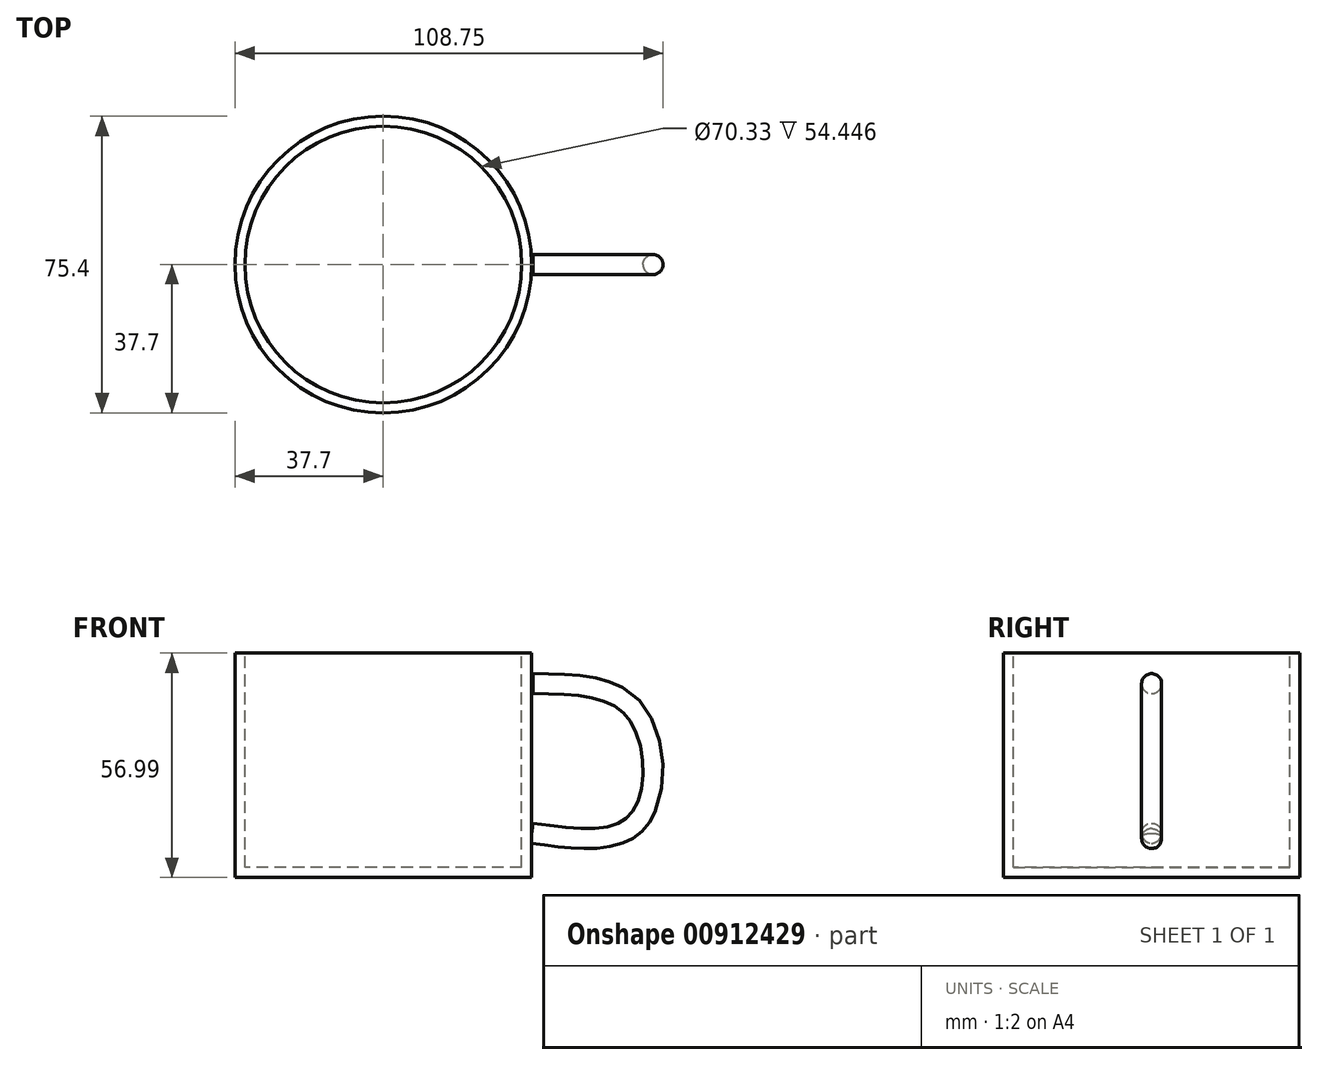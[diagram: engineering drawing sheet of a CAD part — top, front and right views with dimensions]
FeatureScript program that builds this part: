
annotation { "Feature Type Name" : "Feature", "Feature Type Description" : "" }
export const myFeature = defineFeature(function(context is Context, id is Id, definition is map)
    precondition{}
    {
        {
            var Q0;
            Q0=qCreatedBy(makeId("Front.planeOp"),FACE);
            var sketch = newSketch(context, id + "F0", { "sketchPlane" : qUnion([Q0])});
            skLineSegment(sketch, "E0.bottom", {"start": v(0, 64.9) * mm, "end": v(37.7, 64.9) * mm});
            skLineSegment(sketch, "E0.top", {"start": v(0, 7.91) * mm, "end": v(37.7, 7.91) * mm});
            skLineSegment(sketch, "E0.left", {"start": v(0, 64.9) * mm, "end": v(0, 7.91) * mm});
            skLineSegment(sketch, "E0.right", {"start": v(37.7, 64.9) * mm, "end": v(37.7, 7.91) * mm});
            skSolve(sketch);
        }
        {
            var Q0;
            Q0=makeQuery(id+"F0.imprint","IMPRINT",FACE,{"disambiguationData":[TD([[makeQuery(id+"F0.imprint","IMPRINT",EDGE,{"derivedFrom":sQuery(id+"F0.wireOp",EDGE,"E0.bottom")}),-1.0]])]});
            var Q1;
            Q1=sQuery(id+"F0.wireOp",EDGE,"E0.left");
            revolve(context, id + "F1", {"surfaceOperationType" : NewSurfaceOperationType.NEW, "entities" : qUnion([Q0]), "axis" : qUnion([Q1]), "revolveType" : RevolveType.FULL});
        }
        {
            var Q0;
            Q0=makeQuery(id+"F1.opRevolve","SWEPT_FACE",FACE,{"disambiguationData":[OSD([sQuery(id+"F0.wireOp",EDGE,"E0.bottom")])]});
            shell(context, id + "F2", {"entities" : qUnion([Q0]), "thickness" : 2.54 * mm});
        }
        {
            var Q0;
            Q0=qCreatedBy(makeId("Front.planeOp"),FACE);
            var sketch = newSketch(context, id + "F3", { "sketchPlane" : qUnion([Q0])});
            skFitSpline(sketch, "E1", {"points": [v(38, 57.13) * mm, v(64.18, 49.93) * mm, v(64.76, 22.3) * mm, v(37.7, 19.14) * mm], "startDerivative": vector(93.79, -0.65) * mm, "endDerivative": vector(-98.25, 13.93) * mm});
            skSolve(sketch);
        }
        {
            var Q0;
            Q0=sQuery(id+"F3.wireOp",EDGE,"E1");
            var Q1;
            Q1=sQuery(id+"F3.wireOp",VERTEX,"E1.end");
            cPlane(context, id + "F4", {"entities" : qUnion([Q0, Q1]), "cplaneType" : CPlaneType.CURVE_POINT, "offset" : 25.4 * mm, "width" : 152.4 * mm, "height" : 152.4 * mm});
        }
        {
            var Q0;
            Q0=qCreatedBy(id+"F4.planeOp",FACE);
            var sketch = newSketch(context, id + "F5", { "sketchPlane" : qUnion([Q0])});
            skCircle(sketch, "E2", {"center": v(0, 24.24) * mm, "radius": 2.54 * mm});
            skSolve(sketch);
        }
        {
            var Q0;
            Q0=makeQuery(id+"F5.imprint","IMPRINT",FACE,{"disambiguationData":[TD([[makeQuery(id+"F5.imprint","IMPRINT",EDGE,{"derivedFrom":sQuery(id+"F5.wireOp",EDGE,"E2")}),1.0]])]});
            var Q1;
            Q1=sQuery(id+"F3.wireOp",EDGE,"E1");
            sweep(context, id + "F6", {"operationType" : NewBodyOperationType.ADD, "profiles" : qUnion([Q0]), "path" : qUnion([Q1])});
        }
    });
